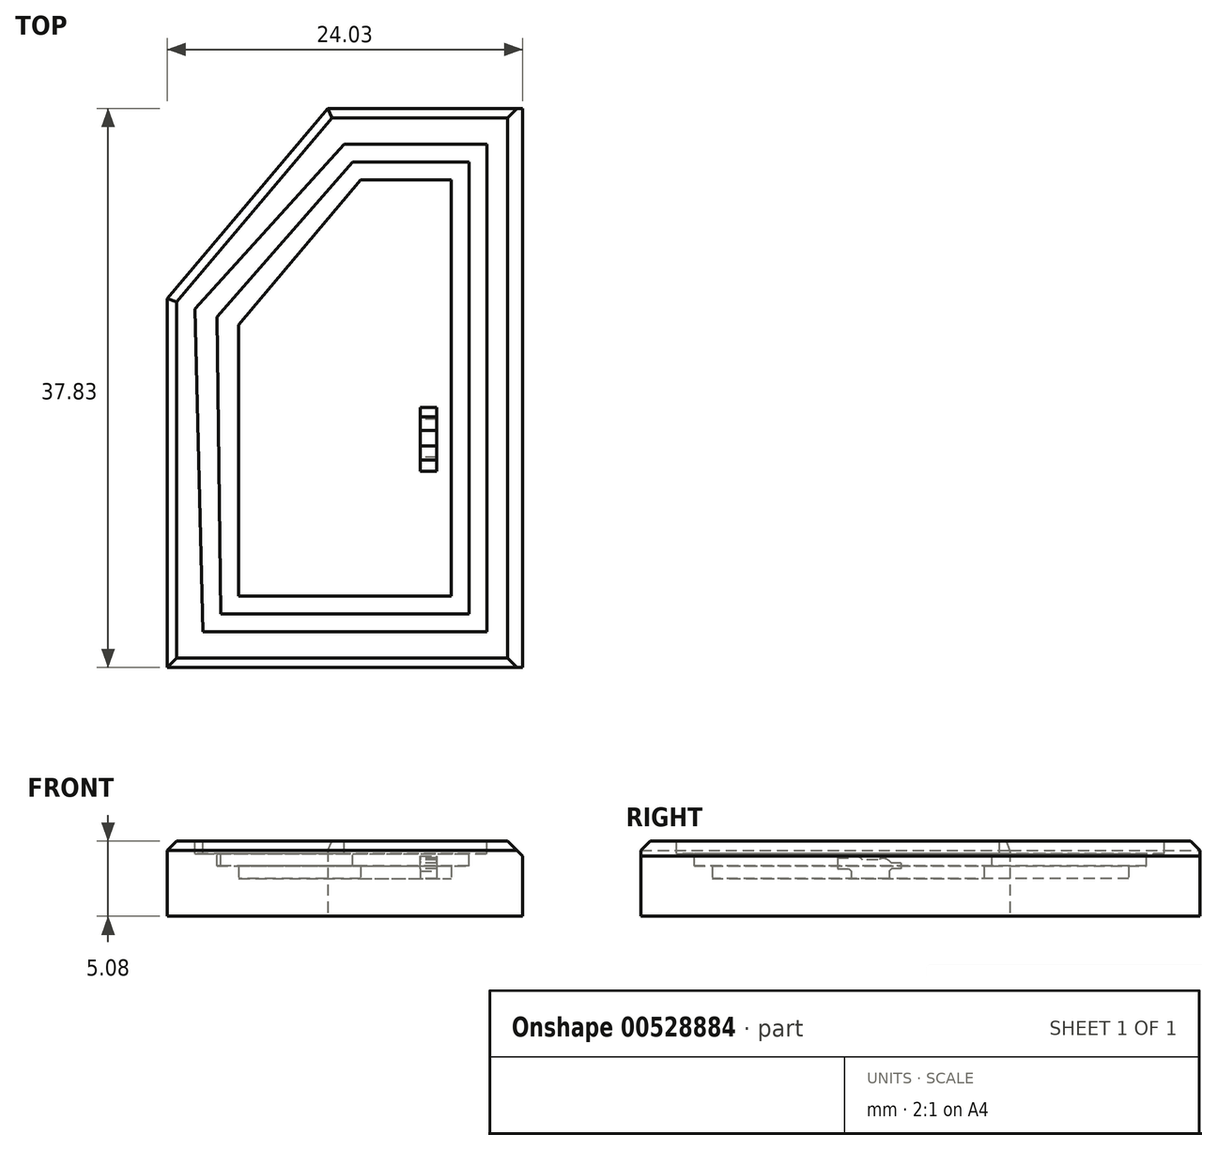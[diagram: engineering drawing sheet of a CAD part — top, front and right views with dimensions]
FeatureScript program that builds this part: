
annotation { "Feature Type Name" : "Feature", "Feature Type Description" : "" }
export const myFeature = defineFeature(function(context is Context, id is Id, definition is map)
    precondition{}
    {
        {
            var Q0;
            Q0=qCreatedBy(makeId("Top.planeOp"),FACE);
            var sketch = newSketch(context, id + "F0", { "sketchPlane" : qUnion([Q0])});
            skLineSegment(sketch, "E0.bottom", {"start": v(-36.19, -42.4) * mm, "end": v(13.77, -42.4) * mm});
            skLineSegment(sketch, "E0.top", {"start": v(-36.19, -4.56) * mm, "end": v(13.77, -4.56) * mm});
            skLineSegment(sketch, "E0.left", {"start": v(-36.19, -42.4) * mm, "end": v(-36.19, -4.56) * mm});
            skLineSegment(sketch, "E0.right", {"start": v(13.77, -42.4) * mm, "end": v(13.77, -4.56) * mm});
            skLineSegment(sketch, "E1", {"start": v(-11.2, -4.56) * mm, "end": v(-11.2, -42.4) * mm});
            skLineSegment(sketch, "E2", {"start": v(-12.16, -4.56) * mm, "end": v(-12.16, -42.4) * mm});
            skLineSegment(sketch, "E3", {"start": v(-25.35, -4.56) * mm, "end": v(-36.19, -17.43) * mm});
            skLineSegment(sketch, "E4", {"start": v(2.23, -4.56) * mm, "end": v(13.77, -17.77) * mm});
            skSolve(sketch);
        }
        {
            var Q0;
            {var subQ0=sQuery(id+"F0.wireOp",EDGE,"E2");Q0=makeQuery(id+"F0.imprint","IMPRINT",FACE,{"disambiguationData":[TD([[makeQuery(id+"F0.imprint","IMPRINT",EDGE,{"derivedFrom":subQ0}),-1.0]])]});}
            var Q1;
            {var subQ4=sQuery(id+"F0.wireOp",EDGE,"E1");Q1=makeQuery(id+"F0.imprint","IMPRINT",FACE,{"disambiguationData":[TD([[makeQuery(id+"F0.imprint","IMPRINT",EDGE,{"derivedFrom":subQ4}),1.0]])]});}
            extrude(context, id + "F1", {"entities" : qUnion([Q0, Q1]), "depth" : 5.08 * mm, "offsetDistance" : 25.4 * mm});
        }
        {
            var Q0;
            Q0=makeQuery(id+"F1.opExtrude","CAP_FACE",FACE,{"disambiguationData":[OSD([sQuery(id+"F0.wireOp",EDGE,"E0.bottom"),sQuery(id+"F0.wireOp",EDGE,"E0.top"),sQuery(id+"F0.wireOp",EDGE,"E0.left"),sQuery(id+"F0.wireOp",EDGE,"E2"),sQuery(id+"F0.wireOp",EDGE,"E3")])],"isStart":false});
            shell(context, id + "F2", {"entities" : qUnion([Q0]), "thickness" : 4.83 * mm});
        }
        {
            var Q0;
            Q0=makeQuery(id+"F2.opShell","OFFSET_FACE",FACE,{"disambiguationData":[OSD([sQuery(id+"F0.wireOp",EDGE,"E0.bottom"),sQuery(id+"F0.wireOp",EDGE,"E0.top"),sQuery(id+"F0.wireOp",EDGE,"E0.left"),sQuery(id+"F0.wireOp",EDGE,"E2"),sQuery(id+"F0.wireOp",EDGE,"E3")])]});
            extrude(context, id + "F3", {"entities" : qUnion([Q0]), "operationType" : NewBodyOperationType.REMOVE, "oppositeDirection" : true, "depth" : 2.54 * mm, "offsetDistance" : 25.4 * mm});
        }
        {
            var Q0;
            Q0=makeQuery(id+"F1.opExtrude","CAP_FACE",FACE,{"disambiguationData":[OSD([sQuery(id+"F0.wireOp",EDGE,"E0.bottom"),sQuery(id+"F0.wireOp",EDGE,"E0.top"),sQuery(id+"F0.wireOp",EDGE,"E0.left"),sQuery(id+"F0.wireOp",EDGE,"E2"),sQuery(id+"F0.wireOp",EDGE,"E3")])],"isStart":false});
            var sketch = newSketch(context, id + "F4", { "sketchPlane" : qUnion([Q0])});
            skLineSegment(sketch, "E5", {"start": v(-33.77, -39.98) * mm, "end": v(-14.57, -39.98) * mm});
            skLineSegment(sketch, "E6", {"start": v(-14.57, -39.98) * mm, "end": v(-14.57, -6.97) * mm});
            skLineSegment(sketch, "E7", {"start": v(-14.57, -6.97) * mm, "end": v(-24.22, -6.97) * mm});
            skLineSegment(sketch, "E8", {"start": v(-24.22, -6.97) * mm, "end": v(-34.3, -18.11) * mm});
            skLineSegment(sketch, "E9", {"start": v(-34.3, -18.11) * mm, "end": v(-33.77, -39.98) * mm});
            skSolve(sketch);
        }
        {
            var Q0;
            Q0=makeQuery(id+"F4.imprint","IMPRINT",FACE,{"disambiguationData":[TD([[makeQuery(id+"F4.imprint","IMPRINT",EDGE,{"derivedFrom":sQuery(id+"F4.wireOp",EDGE,"E5")}),1.0]])]});
            extrude(context, id + "F5", {"entities" : qUnion([Q0]), "operationType" : NewBodyOperationType.REMOVE, "oppositeDirection" : true, "depth" : 0.84 * mm, "offsetDistance" : 25.4 * mm});
        }
        {
            var Q0;
            Q0=makeQuery(id+"F5.boolean.opBoolean","COPY",FACE,{"derivedFrom":makeQuery(id+"F5.opExtrude","CAP_FACE",FACE,{"disambiguationData":[OSD([sQuery(id+"F0.wireOp",EDGE,"E0.bottom"),sQuery(id+"F0.wireOp",EDGE,"E0.top"),sQuery(id+"F0.wireOp",EDGE,"E0.left"),sQuery(id+"F0.wireOp",EDGE,"E2"),sQuery(id+"F0.wireOp",EDGE,"E3"),sQuery(id+"F4.wireOp",EDGE,"E5"),sQuery(id+"F4.wireOp",EDGE,"E6"),sQuery(id+"F4.wireOp",EDGE,"E7"),sQuery(id+"F4.wireOp",EDGE,"E8"),sQuery(id+"F4.wireOp",EDGE,"E9")])],"isStart":false})});
            var sketch = newSketch(context, id + "F6", { "sketchPlane" : qUnion([Q0])});
            skLineSegment(sketch, "E10", {"start": v(-23.66, -8.18) * mm, "end": v(-15.78, -8.18) * mm});
            skLineSegment(sketch, "E11", {"start": v(-15.78, -8.18) * mm, "end": v(-15.78, -38.78) * mm});
            skLineSegment(sketch, "E12", {"start": v(-15.78, -38.78) * mm, "end": v(-32.57, -38.78) * mm});
            skLineSegment(sketch, "E13", {"start": v(-32.57, -38.78) * mm, "end": v(-32.83, -18.65) * mm});
            skLineSegment(sketch, "E14", {"start": v(-32.83, -18.65) * mm, "end": v(-23.66, -8.18) * mm});
            skSolve(sketch);
        }
        {
            var Q0;
            Q0=makeQuery(id+"F6.imprint","IMPRINT",FACE,{"disambiguationData":[TD([[makeQuery(id+"F6.imprint","IMPRINT",EDGE,{"derivedFrom":sQuery(id+"F6.wireOp",EDGE,"E10")}),-1.0]])]});
            extrude(context, id + "F7", {"entities" : qUnion([Q0]), "operationType" : NewBodyOperationType.REMOVE, "oppositeDirection" : true, "depth" : 0.84 * mm, "offsetDistance" : 25.4 * mm});
        }
        {
            var Q0;
            Q0=makeQuery(id+"F3.boolean.opBoolean","COPY",FACE,{"derivedFrom":makeQuery(id+"F3.opExtrude","CAP_FACE",FACE,{"disambiguationData":[OSD([sQuery(id+"F0.wireOp",EDGE,"E0.bottom"),sQuery(id+"F0.wireOp",EDGE,"E0.top"),sQuery(id+"F0.wireOp",EDGE,"E0.left"),sQuery(id+"F0.wireOp",EDGE,"E2"),sQuery(id+"F0.wireOp",EDGE,"E3")])],"isStart":false})});
            extrude(context, id + "F8", {"entities" : qUnion([Q0]), "operationType" : NewBodyOperationType.ADD, "depth" : 0.25 * mm, "offsetDistance" : 25.4 * mm});
        }
        {
            var Q0;
            Q0=makeQuery(id+"F8.opExtrude","CAP_FACE",FACE,{"disambiguationData":[OSD([sQuery(id+"F0.wireOp",EDGE,"E0.bottom"),sQuery(id+"F0.wireOp",EDGE,"E0.top"),sQuery(id+"F0.wireOp",EDGE,"E0.left"),sQuery(id+"F0.wireOp",EDGE,"E2"),sQuery(id+"F0.wireOp",EDGE,"E3")])],"isStart":false});
            var sketch = newSketch(context, id + "F9", { "sketchPlane" : qUnion([Q0])});
            skLineSegment(sketch, "E15.bottom", {"start": v(-17.97, -25.6) * mm, "end": v(-19.08, -25.6) * mm});
            skLineSegment(sketch, "E15.top", {"start": v(-17.97, -28.16) * mm, "end": v(-19.08, -28.16) * mm});
            skLineSegment(sketch, "E15.left", {"start": v(-17.97, -25.6) * mm, "end": v(-17.97, -28.16) * mm});
            skLineSegment(sketch, "E15.right", {"start": v(-19.08, -25.6) * mm, "end": v(-19.08, -28.16) * mm});
            skSolve(sketch);
        }
        {
            var Q0;
            Q0 = qSketchRegion(id + "F9", true);
            extrude(context, id + "F10", {"entities" : qUnion([Q0]), "operationType" : NewBodyOperationType.ADD, "depth" : 1.27 * mm, "offsetDistance" : 25.4 * mm});
        }
        {
            var Q0;
            Q0=makeQuery(id+"F10.opExtrude","CAP_EDGE",EDGE,{"disambiguationData":[OSD([sQuery(id+"F9.wireOp",EDGE,"E15.bottom")])],"isStart":false});
            var Q1;
            Q1=makeQuery(id+"F10.opExtrude","CAP_EDGE",EDGE,{"disambiguationData":[OSD([sQuery(id+"F9.wireOp",EDGE,"E15.top")])],"isStart":false});
            chamfer(context, id + "F11", {"entities" : qUnion([Q0, Q1]), "width" : 0.76 * mm, "tangentPropagation" : true});
        }
        {
            var Q0;
            Q0=makeQuery(id+"F11.opChamfer","BLEND_FACE",FACE,{"disambiguationData":[OSD([sQuery(id+"F9.wireOp",EDGE,"E15.top")])]});
            extrude(context, id + "F12", {"entities" : qUnion([Q0]), "operationType" : NewBodyOperationType.ADD, "depth" : 0.76 * mm, "offsetDistance" : 25.4 * mm});
        }
        {
            var Q0;
            Q0=makeQuery(id+"F12.opExtrude","CAP_EDGE",EDGE,{"disambiguationData":[OSD([sQuery(id+"F9.wireOp",EDGE,"E15.top")])],"isStart":false});
            chamfer(context, id + "F13", {"entities" : qUnion([Q0]), "width" : 0.5 * mm, "tangentPropagation" : true});
        }
        {
            var Q0;
            Q0=makeQuery(id+"F11.opChamfer","BLEND_FACE",FACE,{"disambiguationData":[OSD([sQuery(id+"F9.wireOp",EDGE,"E15.bottom")])]});
            extrude(context, id + "F14", {"entities" : qUnion([Q0]), "operationType" : NewBodyOperationType.ADD, "depth" : 0.5 * mm, "offsetDistance" : 25.4 * mm});
        }
        {
            var Q0;
            Q0=makeQuery(id+"F14.opExtrude","CAP_EDGE",EDGE,{"disambiguationData":[OSD([sQuery(id+"F9.wireOp",EDGE,"E15.bottom")])],"isStart":false});
            chamfer(context, id + "F15", {"entities" : qUnion([Q0]), "width" : 0.25 * mm, "tangentPropagation" : true});
        }
        {
            var Q0;
            Q0=makeQuery(id+"F15.opChamfer","BLEND_FACE",FACE,{"disambiguationData":[OSD([sQuery(id+"F9.wireOp",EDGE,"E15.bottom")])]});
            extrude(context, id + "F16", {"entities" : qUnion([Q0]), "operationType" : NewBodyOperationType.ADD, "depth" : 0.64 * mm, "offsetDistance" : 25.4 * mm});
        }
        {
            var Q0;
            Q0=makeQuery(id+"F13.opChamfer","BLEND_FACE",FACE,{"disambiguationData":[OSD([sQuery(id+"F9.wireOp",EDGE,"E15.top")])]});
            extrude(context, id + "F17", {"entities" : qUnion([Q0]), "operationType" : NewBodyOperationType.ADD, "depth" : 0.76 * mm, "offsetDistance" : 25.4 * mm});
        }
        {
            var Q0;
            Q0=makeQuery(id+"F12.opExtrude","CAP_EDGE",EDGE,{"disambiguationData":[OSD([sQuery(id+"F9.wireOp",EDGE,"E15.bottom"),sQuery(id+"F9.wireOp",EDGE,"E15.top"),sQuery(id+"F9.wireOp",EDGE,"E15.left"),sQuery(id+"F9.wireOp",EDGE,"E15.right")])],"isStart":false});
            var Q1;
            Q1=makeQuery(id+"F14.opExtrude","CAP_EDGE",EDGE,{"disambiguationData":[OSD([sQuery(id+"F9.wireOp",EDGE,"E15.bottom"),sQuery(id+"F9.wireOp",EDGE,"E15.top"),sQuery(id+"F9.wireOp",EDGE,"E15.left"),sQuery(id+"F9.wireOp",EDGE,"E15.right")])],"isStart":false});
            fillet(context, id + "F18", {"entities" : qUnion([Q0, Q1]), "radius" : 0.64 * mm, "tangentPropagation" : true, "allowEdgeOverflow" : false});
        }
        {
            var Q0;
            Q0=makeQuery(id+"F1.opExtrude","SWEPT_BODY",BODY,{"disambiguationData":[OSD([sQuery(id+"F0.wireOp",EDGE,"E0.bottom"),sQuery(id+"F0.wireOp",EDGE,"E0.top"),sQuery(id+"F0.wireOp",EDGE,"E0.right"),sQuery(id+"F0.wireOp",EDGE,"E1"),sQuery(id+"F0.wireOp",EDGE,"E4")])]});
            deleteBodies(context, id + "F19", {"entities" : qUnion([Q0])});
        }
        {
            var Q0;
            {var subQ0=sQuery(id+"F0.wireOp",EDGE,"E0.top");Q0=makeQuery(id+"F1.opExtrude","CAP_EDGE",EDGE,{"disambiguationData":[OSD([subQ0]),TDD([makeQuery(id+"F0.imprint","IMPRINT",EDGE,{"disambiguationData":[TD([[makeQuery(id+"F0.imprint","INTERSECT",VERTEX,{"derivedFrom":[subQ0,sQuery(id+"F0.wireOp",EDGE,"E2")]}),1.0]])],"derivedFrom":subQ0})])],"isStart":false});}
            var Q1;
            Q1=makeQuery(id+"F1.opExtrude","CAP_EDGE",EDGE,{"disambiguationData":[OSD([sQuery(id+"F0.wireOp",EDGE,"E3")])],"isStart":false});
            var Q2;
            Q2=makeQuery(id+"F1.opExtrude","CAP_EDGE",EDGE,{"disambiguationData":[OSD([sQuery(id+"F0.wireOp",EDGE,"E0.left")])],"isStart":false});
            var Q3;
            {var subQ0=sQuery(id+"F0.wireOp",EDGE,"E0.bottom");Q3=makeQuery(id+"F1.opExtrude","CAP_EDGE",EDGE,{"disambiguationData":[OSD([subQ0]),TDD([makeQuery(id+"F0.imprint","IMPRINT",EDGE,{"disambiguationData":[TD([[makeQuery(id+"F0.imprint","INTERSECT",VERTEX,{"derivedFrom":[subQ0,sQuery(id+"F0.wireOp",EDGE,"E0.left")]}),-1.0]])],"derivedFrom":subQ0})])],"isStart":false});}
            chamfer(context, id + "F20", {"entities" : qUnion([Q0, Q1, Q2, Q3]), "width" : 0.64 * mm, "tangentPropagation" : true});
        }
        {
            var Q0;
            Q0=makeQuery(id+"F1.opExtrude","CAP_EDGE",EDGE,{"disambiguationData":[OSD([sQuery(id+"F0.wireOp",EDGE,"E2")])],"isStart":false});
            chamfer(context, id + "F21", {"entities" : qUnion([Q0]), "width" : 1.02 * mm, "tangentPropagation" : true});
        }
    });
